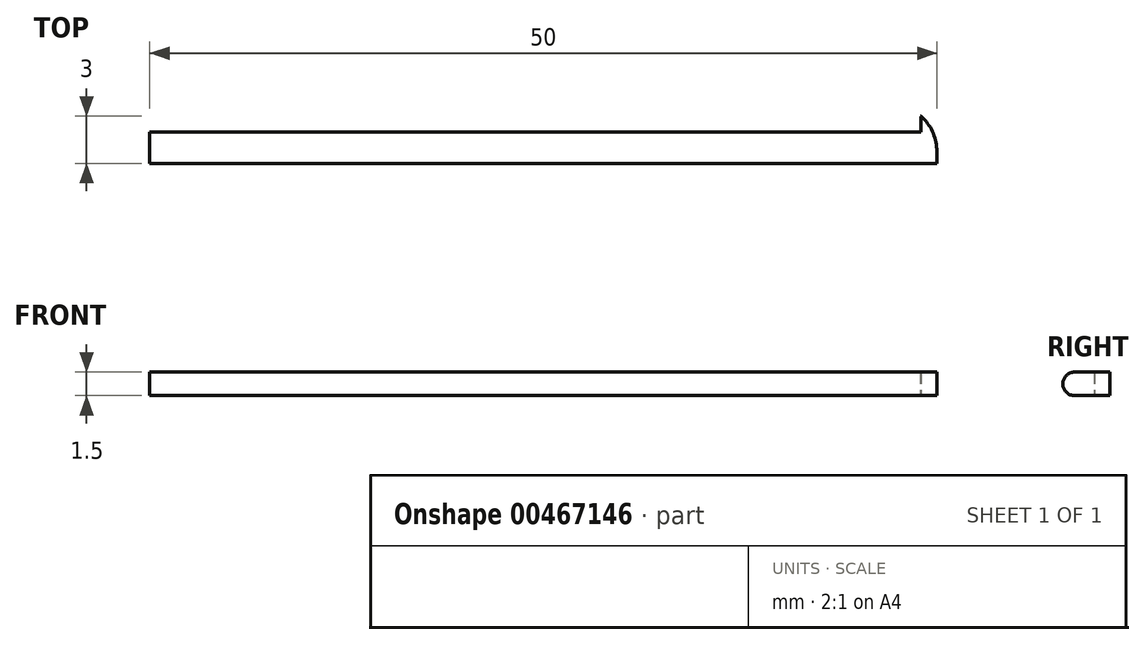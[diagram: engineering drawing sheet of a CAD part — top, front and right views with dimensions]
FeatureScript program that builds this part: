
annotation { "Feature Type Name" : "Feature", "Feature Type Description" : "" }
export const myFeature = defineFeature(function(context is Context, id is Id, definition is map)
    precondition{}
    {
        {
            var Q0;
            Q0=qCreatedBy(makeId("Top.planeOp"),FACE);
            var sketch = newSketch(context, id + "F0", { "sketchPlane" : qUnion([Q0])});
            skLineSegment(sketch, "E0.bottom", {"start": v(25, -1) * mm, "end": v(-25, -1) * mm});
            skLineSegment(sketch, "E0.top", {"start": v(25, 1) * mm, "end": v(-25, 1) * mm});
            skLineSegment(sketch, "E0.left", {"start": v(25, -1) * mm, "end": v(25, -0.24) * mm});
            skLineSegment(sketch, "E0.right", {"start": v(-25, -1) * mm, "end": v(-25, 1) * mm});
            skPoint(sketch, "E0.middle", {"position": v(0, 0) * mm});
            skLineSegment(sketch, "E1", {"start": v(24, 1) * mm, "end": v(24, 2) * mm});
            skLineSegment(sketch, "E2", {"start": v(24, 2) * mm, "end": v(24.12, 1.88) * mm});
            skPoint(sketch, "E3.visualSharp", {"position": v(25, 1) * mm});
            skArc(sketch, "E3.filletArc", {"start": v(25, -0.24) * mm, "mid": v(24.77, 0.9) * mm, "end": v(24.12, 1.88) * mm});
            skLineSegment(sketch, "E4", {"start": v(24, 2) * mm, "end": v(23.95, 2) * mm});
            skArc(sketch, "E5", {"start": v(24, 1.95) * mm, "mid": v(23.99, 1.99) * mm, "end": v(23.95, 2) * mm});
            skSolve(sketch);
        }
        {
            var Q0;
            Q0=makeQuery(id+"F0.imprint","IMPRINT",FACE,{"disambiguationData":[TD([[makeQuery(id+"F0.imprint","IMPRINT",EDGE,{"derivedFrom":sQuery(id+"F0.wireOp",EDGE,"E0.bottom")}),-1.0]])]});
            var Q1;
            {var subQ0=sQuery(id+"F0.wireOp",EDGE,"E1");Q1=makeQuery(id+"F0.imprint","IMPRINT",FACE,{"disambiguationData":[TD([[makeQuery(id+"F0.imprint","IMPRINT",EDGE,{"derivedFrom":subQ0}),-1.0]])]});}
            var Q2;
            {var subQ0=sQuery(id+"F0.wireOp",EDGE,"E4");Q2=makeQuery(id+"F0.imprint","IMPRINT",FACE,{"disambiguationData":[TD([[makeQuery(id+"F0.imprint","IMPRINT",EDGE,{"derivedFrom":subQ0}),1.0]])]});}
            extrude(context, id + "F1", {"entities" : qUnion([Q0, Q1, Q2]), "endBound" : BoundingType.SYMMETRIC, "depth" : 1.5 * mm, "offsetDistance" : 25 * mm});
        }
        {
            var Q0;
            Q0=makeQuery(id+"F1.opExtrude","SWEPT_FACE",FACE,{"disambiguationData":[OSD([sQuery(id+"F0.wireOp",EDGE,"E0.right")])]});
            var sketch = newSketch(context, id + "F2", { "sketchPlane" : qUnion([Q0])});
            skLineSegment(sketch, "E6", {"start": v(0.25, 0.75) * mm, "end": v(0.25, -0.75) * mm});
            skCircle(sketch, "E7", {"center": v(0.25, 0) * mm, "radius": 0.75 * mm});
            skSolve(sketch);
        }
        {
            var Q0;
            {var subQ0=sQuery(id+"F2.wireOp",EDGE,"E7");var subQ1=sQuery(id+"F0.wireOp",EDGE,"E0.right");var subQ2=makeQuery(id+"F1.opExtrude","CAP_EDGE",EDGE,{"disambiguationData":[OSD([subQ1])],"isStart":false});var subQ3=makeQuery(id+"F2.imprint","INTERSECT",VERTEX,{"derivedFrom":[subQ2,sQuery(id+"F2.wireOp",EDGE,"E6"),subQ0]});Q0=makeQuery(id+"F2.imprint","IMPRINT",FACE,{"disambiguationData":[TD([[makeQuery(id+"F2.imprint","IMPRINT",EDGE,{"disambiguationData":[TD([[subQ3,1.0]])],"derivedFrom":subQ0}),-1.0]])]});}
            var Q1;
            {var subQ0=sQuery(id+"F2.wireOp",EDGE,"E7");var subQ1=sQuery(id+"F0.wireOp",EDGE,"E0.right");var subQ2=makeQuery(id+"F1.opExtrude","CAP_EDGE",EDGE,{"disambiguationData":[OSD([subQ1])],"isStart":true});var subQ3=makeQuery(id+"F2.imprint","INTERSECT",VERTEX,{"derivedFrom":[subQ2,sQuery(id+"F2.wireOp",EDGE,"E6"),subQ0]});Q1=makeQuery(id+"F2.imprint","IMPRINT",FACE,{"disambiguationData":[TD([[makeQuery(id+"F2.imprint","IMPRINT",EDGE,{"disambiguationData":[TD([[subQ3,-1.0]])],"derivedFrom":subQ0}),-1.0]])]});}
            extrude(context, id + "F3", {"entities" : qUnion([Q0, Q1]), "operationType" : NewBodyOperationType.REMOVE, "endBound" : BoundingType.THROUGH_ALL, "oppositeDirection" : true, "depth" : 25 * mm, "offsetDistance" : 25 * mm});
        }
    });
